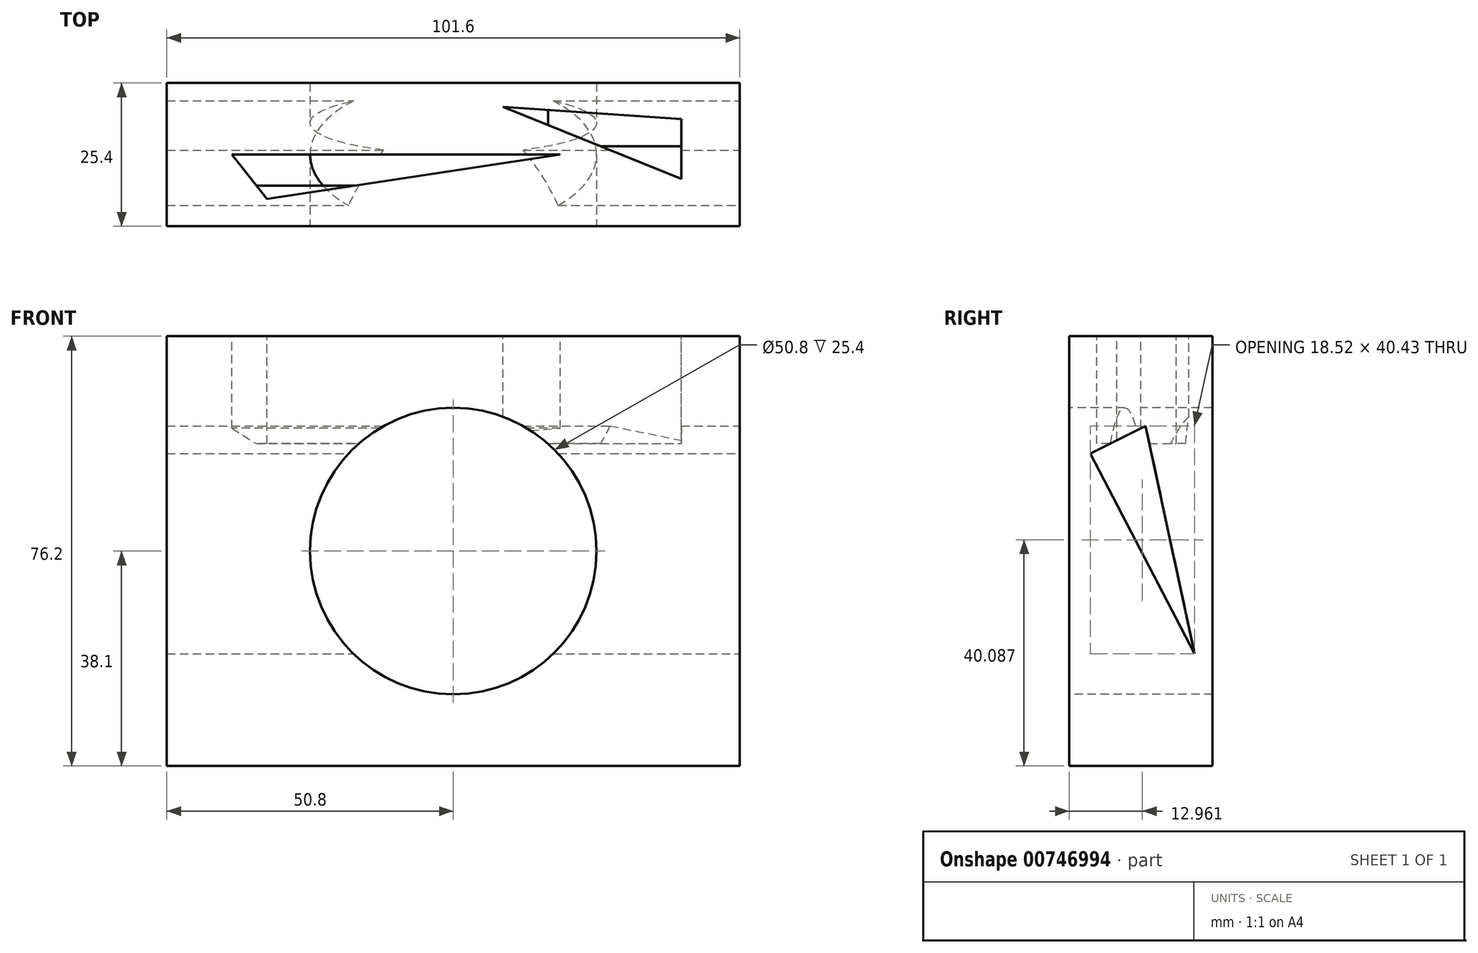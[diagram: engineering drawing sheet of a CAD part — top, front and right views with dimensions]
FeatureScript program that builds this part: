
annotation { "Feature Type Name" : "Feature", "Feature Type Description" : "" }
export const myFeature = defineFeature(function(context is Context, id is Id, definition is map)
    precondition{}
    {
        {
            var Q0;
            Q0=qCreatedBy(makeId("Front.planeOp"),FACE);
            var sketch = newSketch(context, id + "F0", { "sketchPlane" : qUnion([Q0])});
            skLineSegment(sketch, "E0.bottom", {"start": v(0, 0) * mm, "end": v(101.6, 0) * mm});
            skLineSegment(sketch, "E0.top", {"start": v(0, 76.2) * mm, "end": v(101.6, 76.2) * mm});
            skLineSegment(sketch, "E0.left", {"start": v(0, 0) * mm, "end": v(0, 76.2) * mm});
            skLineSegment(sketch, "E0.right", {"start": v(101.6, 0) * mm, "end": v(101.6, 76.2) * mm});
            skSolve(sketch);
        }
        {
            var Q0;
            Q0 = qSketchRegion(id + "F0", true);
            extrude(context, id + "F1", {"entities" : qUnion([Q0]), "depth" : 25.4 * mm, "offsetDistance" : 25.4 * mm});
        }
        {
            var Q0;
            Q0=makeQuery(id+"F1.opExtrude","CAP_FACE",FACE,{"disambiguationData":[OSD([sQuery(id+"F0.wireOp",EDGE,"E0.bottom"),sQuery(id+"F0.wireOp",EDGE,"E0.top"),sQuery(id+"F0.wireOp",EDGE,"E0.left"),sQuery(id+"F0.wireOp",EDGE,"E0.right")])],"isStart":false});
            var sketch = newSketch(context, id + "F2", { "sketchPlane" : qUnion([Q0])});
            skCircle(sketch, "E1", {"center": v(50.8, 38.1) * mm, "radius": 25.4 * mm});
            skSolve(sketch);
        }
        {
            var Q0;
            Q0=makeQuery(id+"F2.imprint","IMPRINT",FACE,{"disambiguationData":[TD([[makeQuery(id+"F2.imprint","IMPRINT",EDGE,{"derivedFrom":sQuery(id+"F2.wireOp",EDGE,"E1")}),1.0]])]});
            var Q1;
            Q1=sQuery(id+"F2.wireOp",EDGE,"E1");
            extrude(context, id + "F3", {"entities" : qUnion([Q0]), "operationType" : NewBodyOperationType.REMOVE, "surfaceEntities" : qUnion([Q1]), "endBound" : BoundingType.THROUGH_ALL, "oppositeDirection" : true, "depth" : 25.4 * mm, "offsetDistance" : 25.4 * mm});
        }
        {
            var Q0;
            Q0=makeQuery(id+"F1.opExtrude","SWEPT_FACE",FACE,{"disambiguationData":[OSD([sQuery(id+"F0.wireOp",EDGE,"E0.top")])]});
            var sketch = newSketch(context, id + "F4", { "sketchPlane" : qUnion([Q0])});
            skLineSegment(sketch, "E2", {"start": v(11.52, -12.7) * mm, "end": v(69.78, -12.7) * mm});
            skPoint(sketch, "E2.startSnap0", {"position": v(0, -12.7) * mm});
            skLineSegment(sketch, "E3", {"start": v(69.78, -12.7) * mm, "end": v(17.74, -20.55) * mm});
            skLineSegment(sketch, "E4", {"start": v(17.74, -20.55) * mm, "end": v(11.52, -12.7) * mm});
            skSolve(sketch);
        }
        {
            var Q0;
            Q0=makeQuery(id+"F4.imprint","IMPRINT",FACE,{"disambiguationData":[TD([[makeQuery(id+"F4.imprint","IMPRINT",EDGE,{"derivedFrom":sQuery(id+"F4.wireOp",EDGE,"E2")}),-1.0]])]});
            extrude(context, id + "F5", {"entities" : qUnion([Q0]), "operationType" : NewBodyOperationType.REMOVE, "oppositeDirection" : true, "depth" : 19.05 * mm, "offsetDistance" : 25.4 * mm});
        }
        {
            var Q0;
            Q0=makeQuery(id+"F1.opExtrude","SWEPT_FACE",FACE,{"disambiguationData":[OSD([sQuery(id+"F0.wireOp",EDGE,"E0.top")])]});
            var sketch = newSketch(context, id + "F6", { "sketchPlane" : qUnion([Q0])});
            skLineSegment(sketch, "E5", {"start": v(91.2, -16.98) * mm, "end": v(91.2, -6.41) * mm});
            skLineSegment(sketch, "E6", {"start": v(91.2, -16.98) * mm, "end": v(59.6, -4.2) * mm});
            skLineSegment(sketch, "E7", {"start": v(59.6, -4.2) * mm, "end": v(91.2, -6.41) * mm});
            skSolve(sketch);
        }
        {
            var Q0;
            Q0=makeQuery(id+"F6.imprint","IMPRINT",FACE,{"disambiguationData":[TD([[makeQuery(id+"F6.imprint","IMPRINT",EDGE,{"derivedFrom":sQuery(id+"F6.wireOp",EDGE,"E5")}),1.0]])]});
            extrude(context, id + "F7", {"entities" : qUnion([Q0]), "operationType" : NewBodyOperationType.REMOVE, "oppositeDirection" : true, "depth" : 19.05 * mm, "offsetDistance" : 25.4 * mm});
        }
        {
            var Q0;
            Q0=makeQuery(id+"F1.opExtrude","SWEPT_FACE",FACE,{"disambiguationData":[OSD([sQuery(id+"F0.wireOp",EDGE,"E0.right")])]});
            var sketch = newSketch(context, id + "F8", { "sketchPlane" : qUnion([Q0])});
            skLineSegment(sketch, "E8", {"start": v(-11.89, 60.3) * mm, "end": v(-3.18, 19.87) * mm});
            skLineSegment(sketch, "E9", {"start": v(-3.18, 19.87) * mm, "end": v(-21.7, 55.4) * mm});
            skLineSegment(sketch, "E10", {"start": v(-11.89, 60.3) * mm, "end": v(-21.7, 55.4) * mm});
            skSolve(sketch);
        }
        {
            var Q0;
            Q0=makeQuery(id+"F8.imprint","IMPRINT",FACE,{"disambiguationData":[TD([[makeQuery(id+"F8.imprint","IMPRINT",EDGE,{"derivedFrom":sQuery(id+"F8.wireOp",EDGE,"E8")}),-1.0]])]});
            extrude(context, id + "F9", {"entities" : qUnion([Q0]), "operationType" : NewBodyOperationType.REMOVE, "endBound" : BoundingType.THROUGH_ALL, "oppositeDirection" : true, "depth" : 25.4 * mm, "offsetDistance" : 25.4 * mm});
        }
    });
